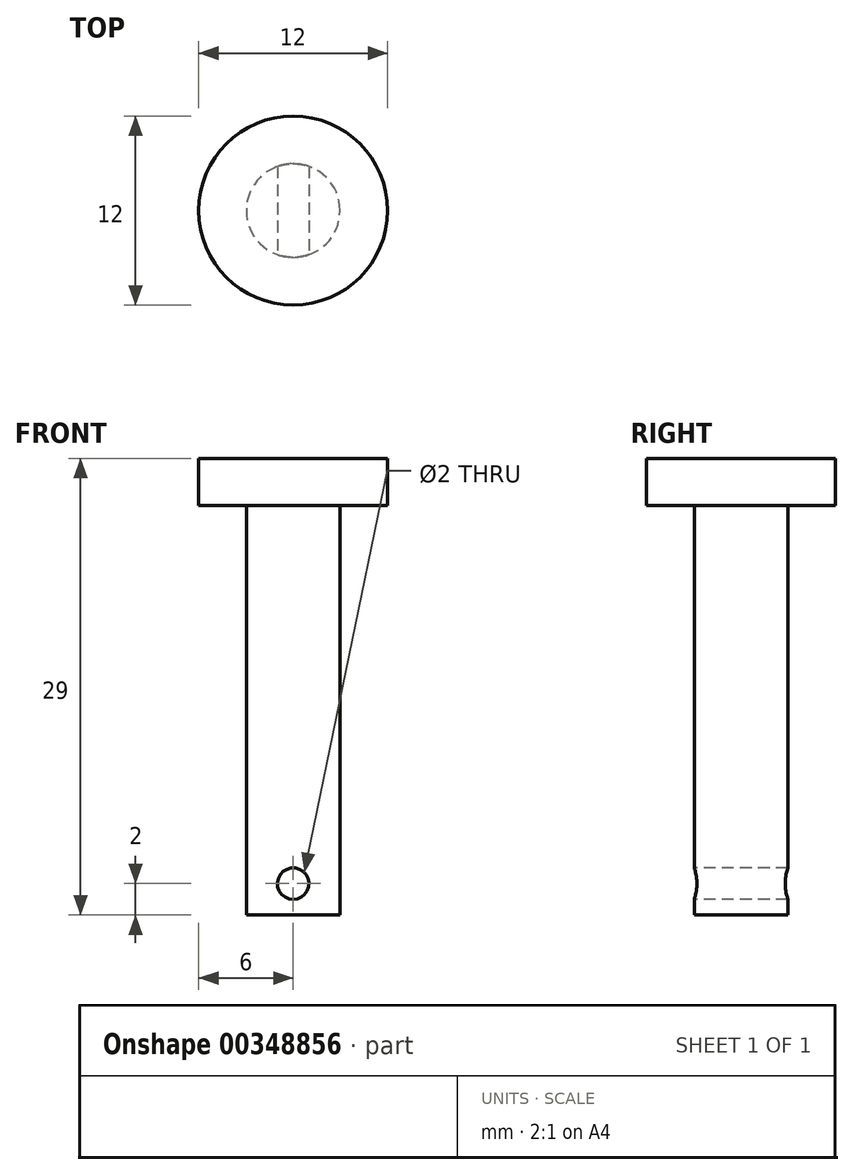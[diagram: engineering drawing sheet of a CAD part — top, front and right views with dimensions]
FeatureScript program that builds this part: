
annotation { "Feature Type Name" : "Feature", "Feature Type Description" : "" }
export const myFeature = defineFeature(function(context is Context, id is Id, definition is map)
    precondition{}
    {
        {
            var Q0;
            Q0=qCreatedBy(makeId("Front.planeOp"),FACE);
            var sketch = newSketch(context, id + "F0", { "sketchPlane" : qUnion([Q0])});
            skLineSegment(sketch, "E0", {"start": v(0, 35.74) * mm, "end": v(0, -6.83) * mm, "construction": true});
            skLineSegment(sketch, "E1", {"start": v(-2.97, 0) * mm, "end": v(-2.97, 26) * mm});
            skLineSegment(sketch, "E2", {"start": v(-2.97, 26) * mm, "end": v(-6, 26) * mm});
            skLineSegment(sketch, "E3", {"start": v(-6, 26) * mm, "end": v(-6, 29) * mm});
            skLineSegment(sketch, "E4", {"start": v(-6, 29) * mm, "end": v(0, 29) * mm});
            skLineSegment(sketch, "E5", {"start": v(-2.97, 0) * mm, "end": v(0, 0) * mm});
            skLineSegment(sketch, "E6", {"start": v(0, 29) * mm, "end": v(0, 0) * mm});
            skSolve(sketch);
        }
        {
            var Q0;
            Q0=makeQuery(id+"F0.imprint","IMPRINT",FACE,{"disambiguationData":[TD([[makeQuery(id+"F0.imprint","IMPRINT",EDGE,{"derivedFrom":sQuery(id+"F0.wireOp",EDGE,"E1")}),-1.0]])]});
            var Q1;
            Q1=sQuery(id+"F0.wireOp",EDGE,"E0");
            revolve(context, id + "F1", {"entities" : qUnion([Q0]), "axis" : qUnion([Q1]), "revolveType" : RevolveType.FULL});
        }
        {
            var Q0;
            Q0=qCreatedBy(makeId("Front.planeOp"),FACE);
            var sketch = newSketch(context, id + "F2", { "sketchPlane" : qUnion([Q0])});
            skCircle(sketch, "E7", {"center": v(0, 2) * mm, "radius": 1 * mm});
            skSolve(sketch);
        }
        {
            var Q0;
            Q0=qSketchRegion(id+"F2",true);
            extrude(context, id + "F3", {"entities" : qUnion([Q0]), "operationType" : NewBodyOperationType.REMOVE, "endBound" : BoundingType.SYMMETRIC, "oppositeDirection" : true, "depth" : 25 * mm});
        }
    });
